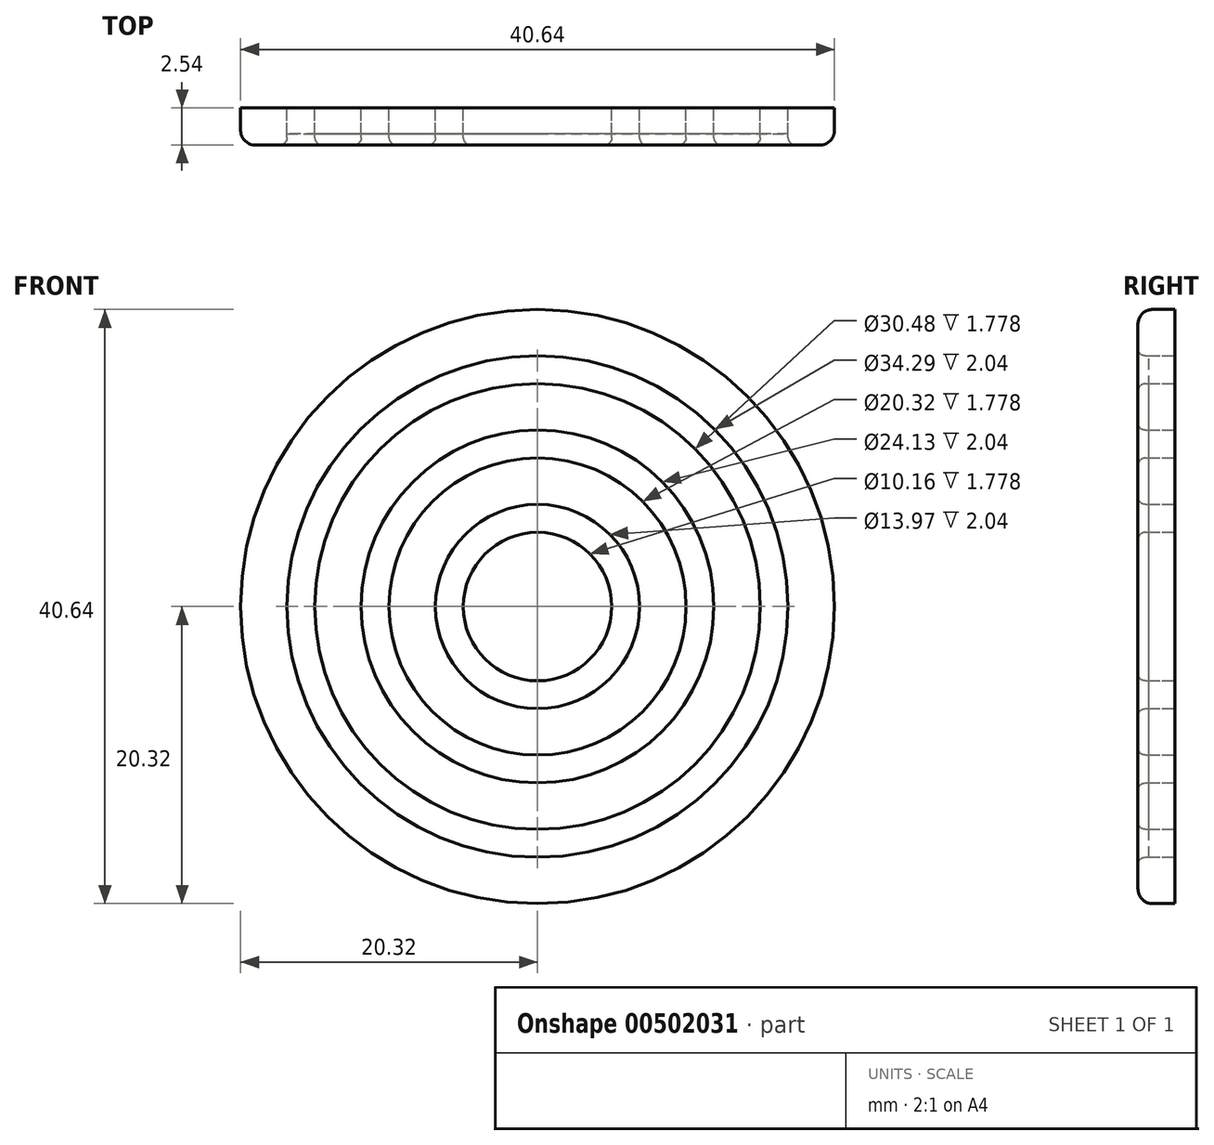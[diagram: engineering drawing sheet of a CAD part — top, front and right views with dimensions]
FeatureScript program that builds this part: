
annotation { "Feature Type Name" : "Feature", "Feature Type Description" : "" }
export const myFeature = defineFeature(function(context is Context, id is Id, definition is map)
    precondition{}
    {
        {
            var Q0;
            Q0=qCreatedBy(makeId("Front.planeOp"),FACE);
            var sketch = newSketch(context, id + "F0", { "sketchPlane" : qUnion([Q0])});
            skCircle(sketch, "E0", {"center": v(0, 0) * mm, "radius": 20.32 * mm});
            skCircle(sketch, "E1", {"center": v(0, 0) * mm, "radius": 15.24 * mm});
            skCircle(sketch, "E2", {"center": v(0, 0) * mm, "radius": 17.15 * mm});
            skCircle(sketch, "E3", {"center": v(0, 0) * mm, "radius": 12.07 * mm});
            skCircle(sketch, "E4", {"center": v(0, 0) * mm, "radius": 10.16 * mm});
            skCircle(sketch, "E5", {"center": v(0, 0) * mm, "radius": 6.99 * mm});
            skCircle(sketch, "E6", {"center": v(0, 0) * mm, "radius": 5.08 * mm});
            skSolve(sketch);
        }
        {
            var Q0;
            Q0=makeQuery(id+"F0.imprint","IMPRINT",FACE,{"disambiguationData":[TD([[makeQuery(id+"F0.imprint","IMPRINT",EDGE,{"derivedFrom":sQuery(id+"F0.wireOp",EDGE,"E0")}),1.0]])]});
            var Q1;
            Q1=makeQuery(id+"F0.imprint","IMPRINT",FACE,{"disambiguationData":[TD([[makeQuery(id+"F0.imprint","IMPRINT",EDGE,{"derivedFrom":sQuery(id+"F0.wireOp",EDGE,"E1")}),1.0]])]});
            var Q2;
            Q2=makeQuery(id+"F0.imprint","IMPRINT",FACE,{"disambiguationData":[TD([[makeQuery(id+"F0.imprint","IMPRINT",EDGE,{"derivedFrom":sQuery(id+"F0.wireOp",EDGE,"E4")}),1.0]])]});
            var Q3;
            Q3=makeQuery(id+"F0.imprint","IMPRINT",FACE,{"disambiguationData":[TD([[makeQuery(id+"F0.imprint","IMPRINT",EDGE,{"derivedFrom":sQuery(id+"F0.wireOp",EDGE,"E6")}),1.0]])]});
            extrude(context, id + "F1", {"entities" : qUnion([Q0, Q1, Q2, Q3]), "depth" : 2.54 * mm, "offsetDistance" : 25.4 * mm});
        }
        {
            var Q0;
            Q0=makeQuery(id+"F0.imprint","IMPRINT",FACE,{"disambiguationData":[TD([[makeQuery(id+"F0.imprint","IMPRINT",EDGE,{"derivedFrom":sQuery(id+"F0.wireOp",EDGE,"E1")}),-1.0]])]});
            var Q1;
            Q1=makeQuery(id+"F0.imprint","IMPRINT",FACE,{"disambiguationData":[TD([[makeQuery(id+"F0.imprint","IMPRINT",EDGE,{"derivedFrom":sQuery(id+"F0.wireOp",EDGE,"E3")}),1.0]])]});
            var Q2;
            Q2=makeQuery(id+"F0.imprint","IMPRINT",FACE,{"disambiguationData":[TD([[makeQuery(id+"F0.imprint","IMPRINT",EDGE,{"derivedFrom":sQuery(id+"F0.wireOp",EDGE,"E5")}),1.0]])]});
            extrude(context, id + "F2", {"entities" : qUnion([Q0, Q1, Q2]), "depth" : 1.78 * mm, "offsetDistance" : 25.4 * mm});
        }
        {
            var Q0;
            Q0=makeQuery(id+"F1.opExtrude","CAP_EDGE",EDGE,{"disambiguationData":[OSD([sQuery(id+"F0.wireOp",EDGE,"E0")])],"isStart":false});
            fillet(context, id + "F3", {"entities" : qUnion([Q0]), "radius" : 1 * mm, "tangentPropagation" : true, "allowEdgeOverflow" : false});
        }
        {
            var Q0;
            Q0=makeQuery(id+"F1.opExtrude","CAP_EDGE",EDGE,{"disambiguationData":[OSD([sQuery(id+"F0.wireOp",EDGE,"E6")])],"isStart":false});
            var Q1;
            Q1=makeQuery(id+"F1.opExtrude","CAP_EDGE",EDGE,{"disambiguationData":[OSD([sQuery(id+"F0.wireOp",EDGE,"E5")])],"isStart":false});
            var Q2;
            Q2=makeQuery(id+"F1.opExtrude","CAP_EDGE",EDGE,{"disambiguationData":[OSD([sQuery(id+"F0.wireOp",EDGE,"E4")])],"isStart":false});
            var Q3;
            Q3=makeQuery(id+"F1.opExtrude","CAP_EDGE",EDGE,{"disambiguationData":[OSD([sQuery(id+"F0.wireOp",EDGE,"E3")])],"isStart":false});
            var Q4;
            Q4=makeQuery(id+"F1.opExtrude","CAP_EDGE",EDGE,{"disambiguationData":[OSD([sQuery(id+"F0.wireOp",EDGE,"E1")])],"isStart":false});
            var Q5;
            Q5=makeQuery(id+"F1.opExtrude","CAP_EDGE",EDGE,{"disambiguationData":[OSD([sQuery(id+"F0.wireOp",EDGE,"E2")])],"isStart":false});
            fillet(context, id + "F4", {"entities" : qUnion([Q0, Q1, Q2, Q3, Q4, Q5]), "radius" : 0.5 * mm, "tangentPropagation" : true, "allowEdgeOverflow" : false});
        }
    });
